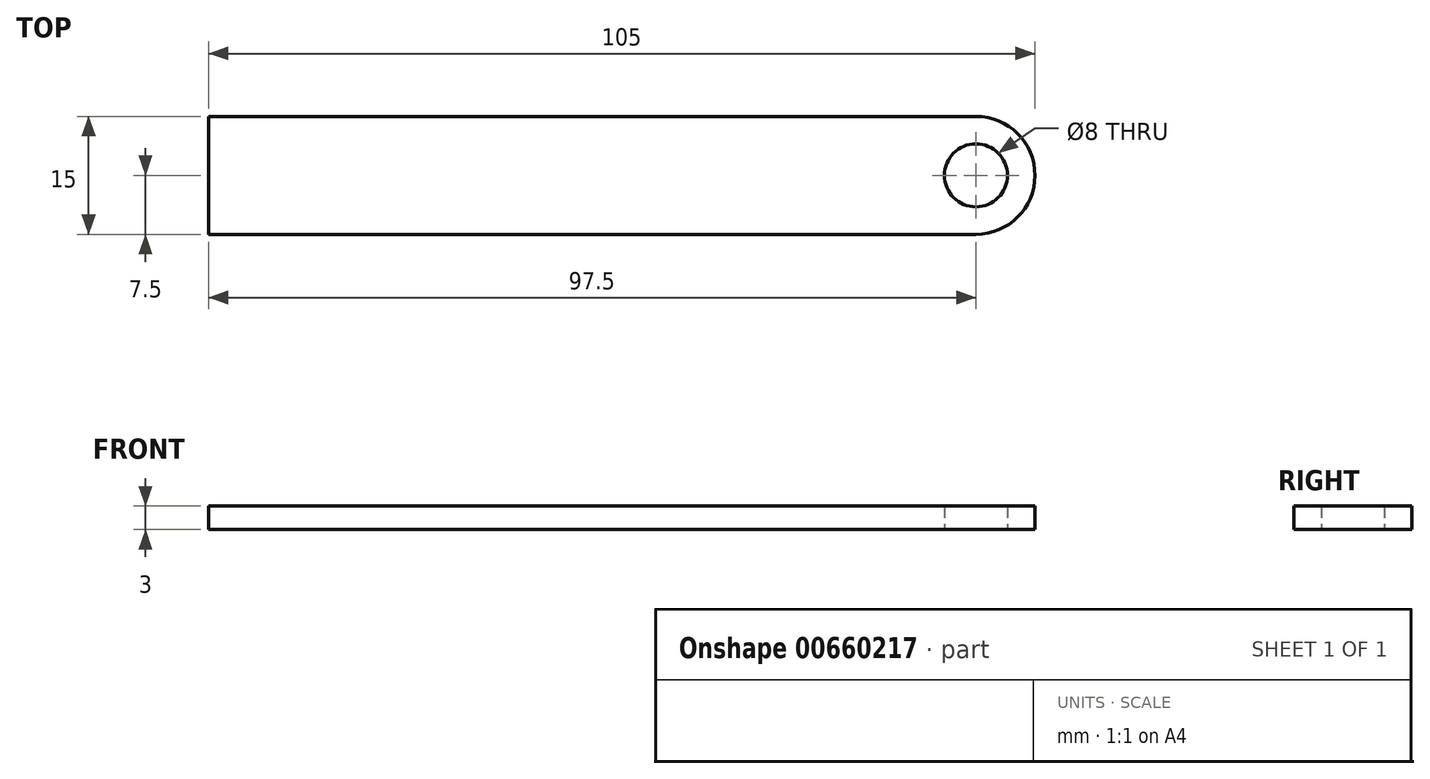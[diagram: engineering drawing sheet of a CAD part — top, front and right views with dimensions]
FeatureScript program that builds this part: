
annotation { "Feature Type Name" : "Feature", "Feature Type Description" : "" }
export const myFeature = defineFeature(function(context is Context, id is Id, definition is map)
    precondition{}
    {
        {
            var Q0;
            Q0=qCreatedBy(makeId("Top.planeOp"),FACE);
            var sketch = newSketch(context, id + "F0", { "sketchPlane" : qUnion([Q0])});
            skLineSegment(sketch, "E0.bottom", {"start": v(12.5, 7.5) * mm, "end": v(85, 7.5) * mm});
            skLineSegment(sketch, "E0.top", {"start": v(12.5, -7.5) * mm, "end": v(85, -7.5) * mm});
            skLineSegment(sketch, "E0.right", {"start": v(92.5, 0) * mm, "end": v(92.5, 0) * mm});
            skCircle(sketch, "E1", {"center": v(85, 0) * mm, "radius": 4 * mm});
            skPoint(sketch, "E2.orphan", {"position": v(0, 26.66) * mm});
            skPoint(sketch, "E3.visualSharp", {"position": v(92.5, 7.5) * mm});
            skArc(sketch, "E3.filletArc", {"start": v(92.5, 0) * mm, "mid": v(90.3, 5.3) * mm, "end": v(85, 7.5) * mm});
            skPoint(sketch, "E4.visualSharp", {"position": v(92.5, -7.5) * mm});
            skArc(sketch, "E4.filletArc", {"start": v(85, -7.5) * mm, "mid": v(90.3, -5.3) * mm, "end": v(92.5, 0) * mm});
            skLineSegment(sketch, "E5.left", {"start": v(-12.5, 7.5) * mm, "end": v(-12.5, -7.5) * mm});
            skPoint(sketch, "E0.left.start.orphan", {"position": v(-7.5, 7.5) * mm});
            skLineSegment(sketch, "E6", {"start": v(12.5, -7.5) * mm, "end": v(-12.5, -7.5) * mm});
            skLineSegment(sketch, "E7", {"start": v(12.5, 7.5) * mm, "end": v(-12.5, 7.5) * mm});
            skSolve(sketch);
        }
        {
            var Q0;
            Q0=makeQuery(id+"F0.imprint","IMPRINT",FACE,{"disambiguationData":[TD([[makeQuery(id+"F0.imprint","IMPRINT",EDGE,{"derivedFrom":sQuery(id+"F0.wireOp",EDGE,"E0.bottom")}),-1.0]])]});
            extrude(context, id + "F1", {"entities" : qUnion([Q0]), "depth" : 3 * mm, "offsetDistance" : 25 * mm});
        }
    });
